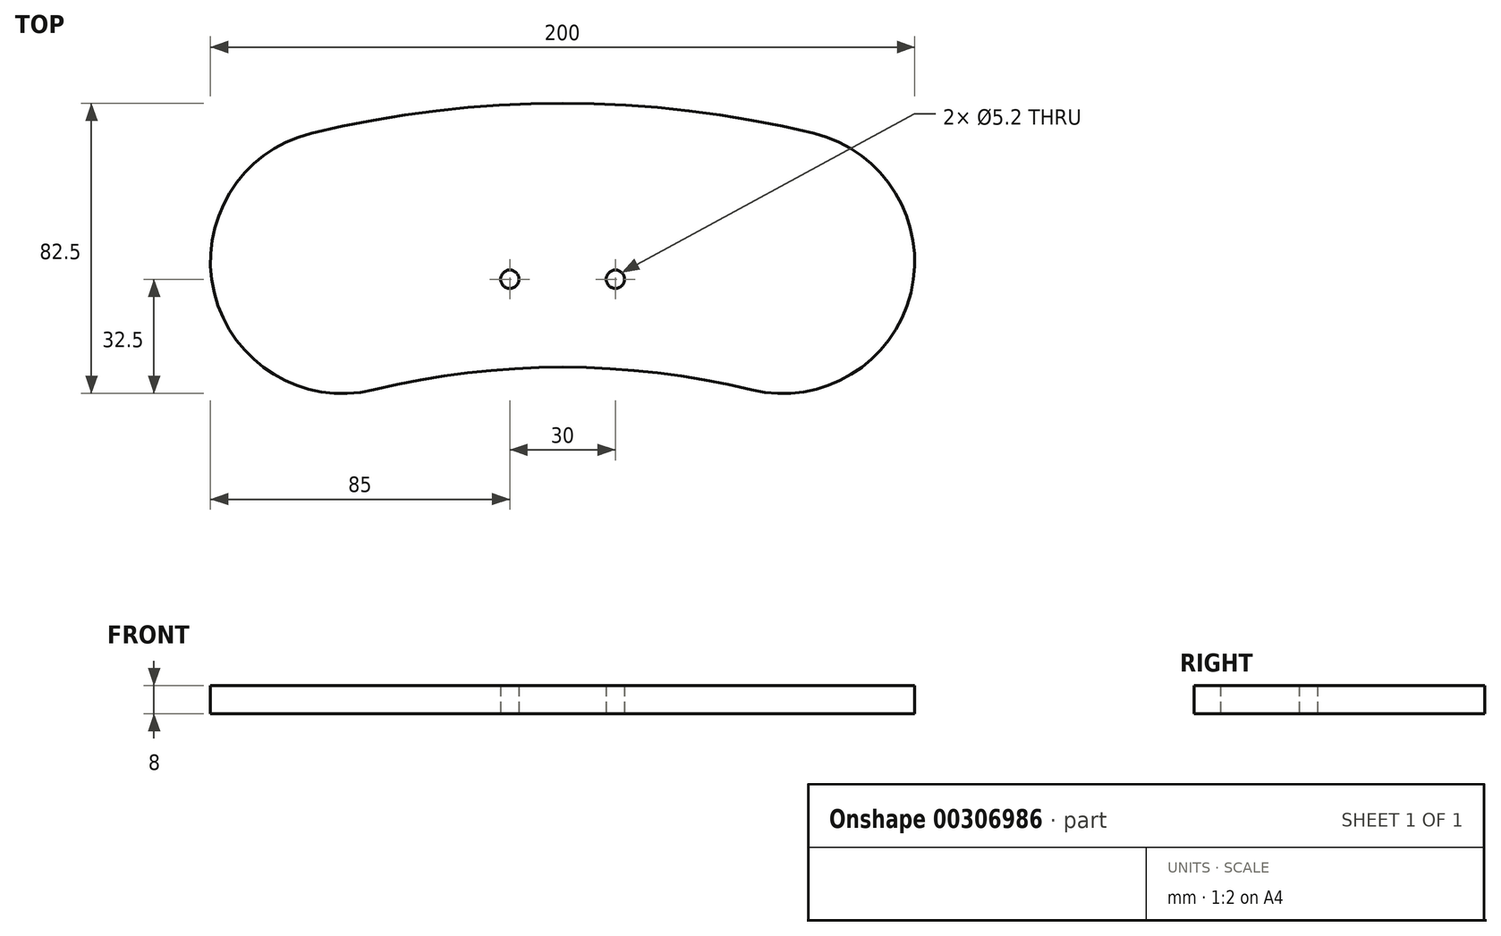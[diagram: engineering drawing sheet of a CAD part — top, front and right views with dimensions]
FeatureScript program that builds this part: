
annotation { "Feature Type Name" : "Feature", "Feature Type Description" : "" }
export const myFeature = defineFeature(function(context is Context, id is Id, definition is map)
    precondition{}
    {
        {
            assignVariable(context, id + "F0", {"name" : "thicknessWood", "anyValue" : 8});
        }
        {
            var Q0;
            Q0=qCreatedBy(makeId("Top.planeOp"),FACE);
            var sketch = newSketch(context, id + "F1", { "sketchPlane" : qUnion([Q0])});
            skLineSegment(sketch, "E0", {"start": v(0, 75) * mm, "end": v(0, 0) * mm, "construction": true});
            skCircle(sketch, "E1", {"center": v(-62.5, 30) * mm, "radius": 37.5 * mm});
            skCircle(sketch, "E2.MirrorC", {"center": v(62.5, 30) * mm, "radius": 37.5 * mm});
            skArc(sketch, "E3", {"start": v(71.37, 66.44) * mm, "mid": v(0, 75) * mm, "end": v(-71.37, 66.44) * mm});
            skArc(sketch, "E4", {"start": v(53.63, -6.44) * mm, "mid": v(0, 0) * mm, "end": v(-53.63, -6.44) * mm});
            skCircle(sketch, "E5", {"center": v(0, 25) * mm, "radius": 2.6 * mm});
            skCircle(sketch, "E6", {"center": v(-50, 20) * mm, "radius": 1.75 * mm});
            skCircle(sketch, "E7.MirrorC", {"center": v(50, 20) * mm, "radius": 1.75 * mm});
            skCircle(sketch, "E8", {"center": v(15, 25) * mm, "radius": 2.6 * mm});
            skCircle(sketch, "E9", {"center": v(-15, 25) * mm, "radius": 2.6 * mm});
            skSolve(sketch);
        }
        {
            var Q0;
            {var subQ0=sQuery(id+"F1.wireOp",EDGE,"E3");Q0=makeQuery(id+"F1.imprint","IMPRINT",FACE,{"disambiguationData":[TD([[makeQuery(id+"F1.imprint","IMPRINT",EDGE,{"derivedFrom":subQ0}),1.0]])]});}
            var Q1;
            Q1=makeQuery(id+"F1.imprint","IMPRINT",FACE,{"disambiguationData":[TD([[makeQuery(id+"F1.imprint","IMPRINT",EDGE,{"derivedFrom":sQuery(id+"F1.wireOp",EDGE,"E6")}),1.0]])]});
            var Q2;
            Q2=makeQuery(id+"F1.imprint","IMPRINT",FACE,{"disambiguationData":[TD([[makeQuery(id+"F1.imprint","IMPRINT",EDGE,{"derivedFrom":sQuery(id+"F1.wireOp",EDGE,"E6")}),-1.0]])]});
            var Q3;
            Q3=makeQuery(id+"F1.imprint","IMPRINT",FACE,{"disambiguationData":[TD([[makeQuery(id+"F1.imprint","IMPRINT",EDGE,{"derivedFrom":sQuery(id+"F1.wireOp",EDGE,"E7.MirrorC")}),1.0]])]});
            var Q4;
            Q4=makeQuery(id+"F1.imprint","IMPRINT",FACE,{"disambiguationData":[TD([[makeQuery(id+"F1.imprint","IMPRINT",EDGE,{"derivedFrom":sQuery(id+"F1.wireOp",EDGE,"E7.MirrorC")}),-1.0]])]});
            var Q5;
            Q5=makeQuery(id+"F1.imprint","IMPRINT",FACE,{"disambiguationData":[TD([[makeQuery(id+"F1.imprint","IMPRINT",EDGE,{"derivedFrom":sQuery(id+"F1.wireOp",EDGE,"E5")}),1.0]])]});
            extrude(context, id + "F2", {"entities" : qUnion([Q0, Q1, Q2, Q3, Q4, Q5]), "depth" : (getVariable(context, 'thicknessWood')) * mm});
        }
    });
